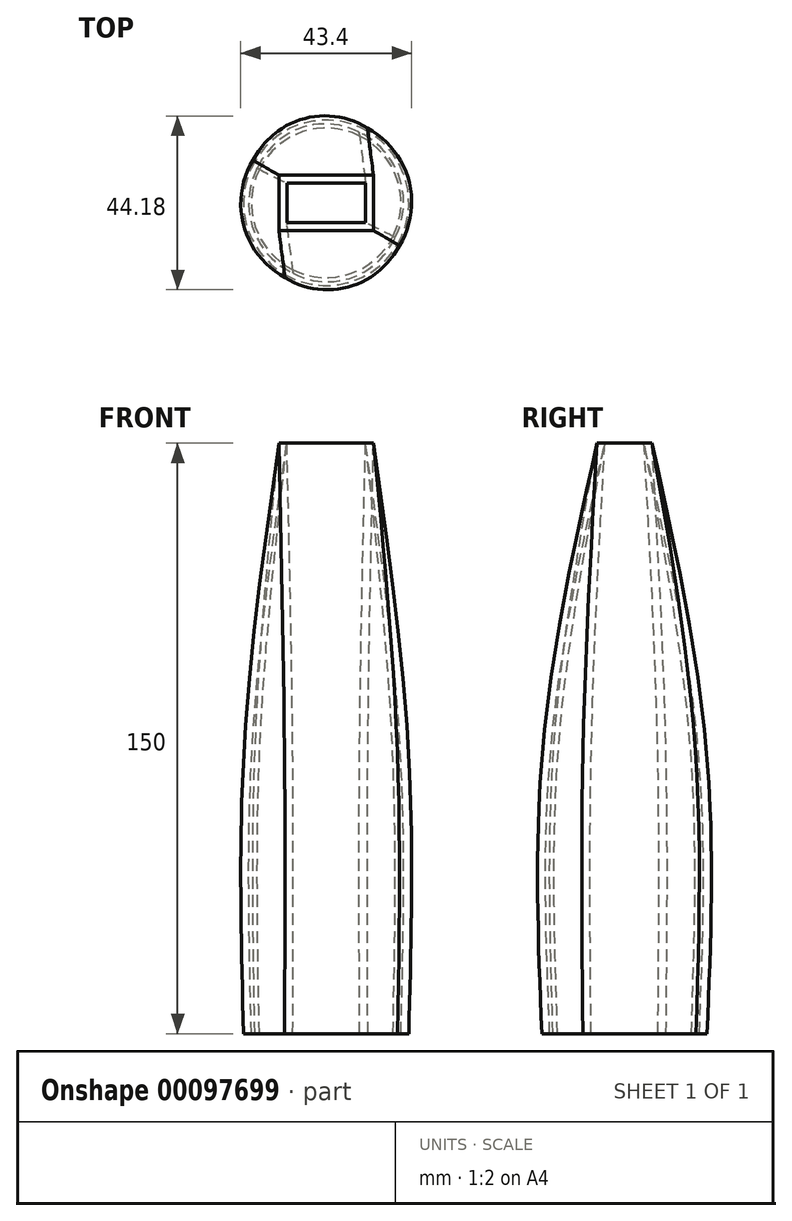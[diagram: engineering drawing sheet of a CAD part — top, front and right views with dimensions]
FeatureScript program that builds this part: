
annotation { "Feature Type Name" : "Feature", "Feature Type Description" : "" }
export const myFeature = defineFeature(function(context is Context, id is Id, definition is map)
    precondition{}
    {
        {
            var Q0;
            Q0=qCreatedBy(makeId("Top.planeOp"),FACE);
            cPlane(context, id + "F0", {"entities" : qUnion([Q0]), "cplaneType" : CPlaneType.OFFSET, "offset" : 70 * mm, "width" : 152.4 * mm, "height" : 152.4 * mm});
        }
        {
            var Q0;
            Q0=qCreatedBy(id+"F0.planeOp",FACE);
            cPlane(context, id + "F1", {"entities" : qUnion([Q0]), "cplaneType" : CPlaneType.OFFSET, "offset" : 80 * mm, "width" : 152.4 * mm, "height" : 152.4 * mm});
        }
        {
            var Q0;
            Q0=qCreatedBy(makeId("Top.planeOp"),FACE);
            var sketch = newSketch(context, id + "F2", { "sketchPlane" : qUnion([Q0])});
            skCircle(sketch, "E0", {"center": v(0, 0) * mm, "radius": 19 * mm});
            skSolve(sketch);
        }
        {
            var Q0;
            Q0=qCreatedBy(id+"F0.planeOp",FACE);
            var sketch = newSketch(context, id + "F3", { "sketchPlane" : qUnion([Q0])});
            skCircle(sketch, "E1", {"center": v(0, 0) * mm, "radius": 18.96 * mm});
            skSolve(sketch);
        }
        {
            var Q0;
            Q0=qCreatedBy(makeId("Top.planeOp"),FACE);
            var sketch = newSketch(context, id + "F4", { "sketchPlane" : qUnion([Q0])});
            skCircle(sketch, "E2", {"center": v(0, 0) * mm, "radius": 21 * mm});
            skSolve(sketch);
        }
        {
            var Q0;
            Q0=qCreatedBy(id+"F0.planeOp",FACE);
            var sketch = newSketch(context, id + "F5", { "sketchPlane" : qUnion([Q0])});
            skCircle(sketch, "E3", {"center": v(0, 0) * mm, "radius": 21 * mm});
            skSolve(sketch);
        }
        {
            var Q0;
            Q0=qCreatedBy(id+"F1.planeOp",FACE);
            var sketch = newSketch(context, id + "F6", { "sketchPlane" : qUnion([Q0])});
            skLineSegment(sketch, "E4.bottom", {"start": v(10, -5) * mm, "end": v(-10, -5) * mm});
            skLineSegment(sketch, "E4.top", {"start": v(10, 5) * mm, "end": v(-10, 5) * mm});
            skLineSegment(sketch, "E4.left", {"start": v(10, -5) * mm, "end": v(10, 5) * mm});
            skLineSegment(sketch, "E4.right", {"start": v(-10, -5) * mm, "end": v(-10, 5) * mm});
            skPoint(sketch, "E4.middle", {"position": v(0, 0) * mm});
            skSolve(sketch);
        }
        {
            var Q0;
            Q0=qCreatedBy(id+"F1.planeOp",FACE);
            var sketch = newSketch(context, id + "F7", { "sketchPlane" : qUnion([Q0])});
            skLineSegment(sketch, "E5.bottom", {"start": v(12, -7) * mm, "end": v(-12, -7) * mm});
            skLineSegment(sketch, "E5.top", {"start": v(12, 7) * mm, "end": v(-12, 7) * mm});
            skLineSegment(sketch, "E5.left", {"start": v(12, -7) * mm, "end": v(12, 7) * mm});
            skLineSegment(sketch, "E5.right", {"start": v(-12, -7) * mm, "end": v(-12, 7) * mm});
            skPoint(sketch, "E5.middle", {"position": v(0, 0) * mm});
            skSolve(sketch);
        }
        {
            var Q0;
            Q0=makeQuery(id+"F4.imprint","IMPRINT",FACE,{"disambiguationData":[TD([[makeQuery(id+"F4.imprint","IMPRINT",EDGE,{"derivedFrom":sQuery(id+"F4.wireOp",EDGE,"E2")}),1.0]])]});
            var Q1;
            Q1=makeQuery(id+"F5.imprint","IMPRINT",FACE,{"disambiguationData":[TD([[makeQuery(id+"F5.imprint","IMPRINT",EDGE,{"derivedFrom":sQuery(id+"F5.wireOp",EDGE,"E3")}),1.0]])]});
            var Q2;
            Q2=makeQuery(id+"F7.imprint","IMPRINT",FACE,{"disambiguationData":[TD([[makeQuery(id+"F7.imprint","IMPRINT",EDGE,{"derivedFrom":sQuery(id+"F7.wireOp",EDGE,"E5.bottom")}),-1.0]])]});
            loft(context, id + "F8", {"sheetProfilesArray" : [{ "sheetProfileEntities" : qUnion([Q0]) }, { "sheetProfileEntities" : qUnion([Q1]) }, { "sheetProfileEntities" : qUnion([Q2]) }]});
        }
        {
            var Q1;
            Q1 = qSketchRegion(id + "F2", true);
            var Q2;
            Q2 = qSketchRegion(id + "F3", true);
            var Q3;
            Q3 = qSketchRegion(id + "F6", true);
            loft(context, id + "F9", {"operationType" : NewBodyOperationType.REMOVE, "sheetProfilesArray" : [{ "sheetProfileEntities" : qUnion([Q1]) }, { "sheetProfileEntities" : qUnion([Q2]) }, { "sheetProfileEntities" : qUnion([Q3]) }]});
        }
    });
